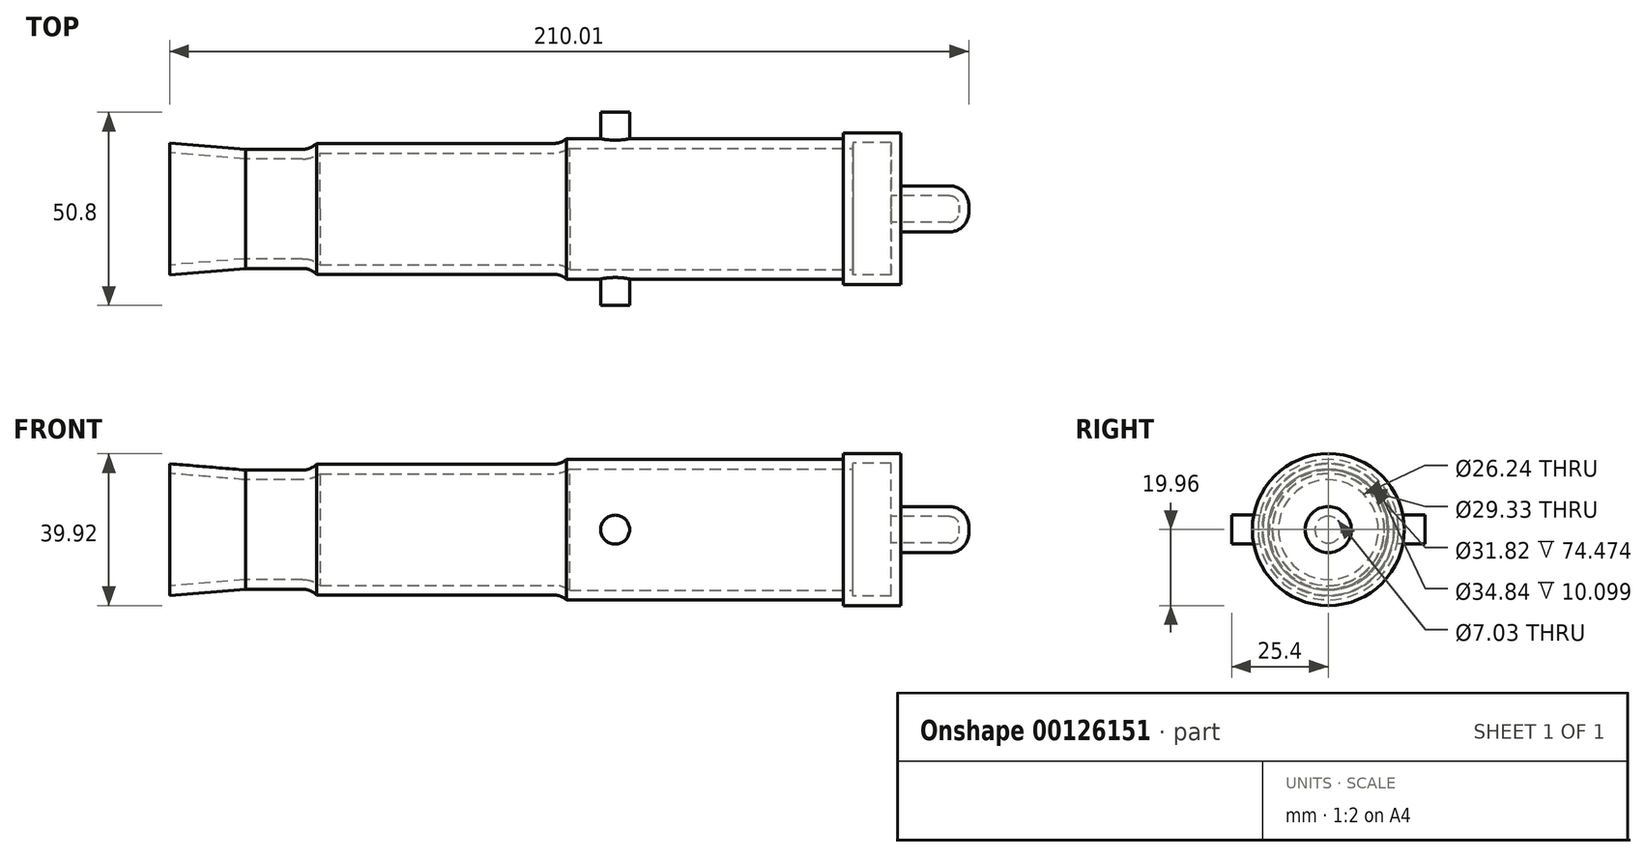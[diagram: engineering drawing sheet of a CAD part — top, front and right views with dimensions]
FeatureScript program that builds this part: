
annotation { "Feature Type Name" : "Feature", "Feature Type Description" : "" }
export const myFeature = defineFeature(function(context is Context, id is Id, definition is map)
    precondition{}
    {
        {
            var Q0;
            Q0=qCreatedBy(makeId("Right.planeOp"),FACE);
            var sketch = newSketch(context, id + "F0", { "sketchPlane" : qUnion([Q0])});
            skCircle(sketch, "E0", {"center": v(0, 0) * mm, "radius": 15.66 * mm});
            skSolve(sketch);
        }
        {
            var Q0;
            Q0 = qSketchRegion(id + "F0", true);
            extrude(context, id + "F1", {"entities" : qUnion([Q0]), "depth" : 157.22 * mm});
        }
        {
            var Q0;
            Q0=makeQuery(id+"F1.opExtrude","CAP_FACE",FACE,{"disambiguationData":[OSD([sQuery(id+"F0.wireOp",EDGE,"E0")])],"isStart":false});
            var sketch = newSketch(context, id + "F2", { "sketchPlane" : qUnion([Q0])});
            skCircle(sketch, "E1", {"center": v(0, 0) * mm, "radius": 17.2 * mm});
            skSolve(sketch);
        }
        {
            var Q0;
            Q0 = qSketchRegion(id + "F2", true);
            extrude(context, id + "F3", {"entities" : qUnion([Q0]), "operationType" : NewBodyOperationType.ADD, "oppositeDirection" : true, "depth" : 138.47 * mm});
        }
        {
            var Q0;
            Q0=makeQuery(id+"F3.boolean.opBoolean","MERGE",FACE,{"derivedFrom":[makeQuery(id+"F1.opExtrude","CAP_FACE",FACE,{"disambiguationData":[OSD([sQuery(id+"F0.wireOp",EDGE,"E0")])],"isStart":false}),makeQuery(id+"F3.opExtrude","CAP_FACE",FACE,{"disambiguationData":[OSD([sQuery(id+"F2.wireOp",EDGE,"E1")])],"isStart":true})]});
            var sketch = newSketch(context, id + "F4", { "sketchPlane" : qUnion([Q0])});
            skCircle(sketch, "E2", {"center": v(0, 0) * mm, "radius": 18.45 * mm});
            skSolve(sketch);
        }
        {
            var Q0;
            Q0 = qSketchRegion(id + "F4", true);
            extrude(context, id + "F5", {"entities" : qUnion([Q0]), "operationType" : NewBodyOperationType.ADD, "oppositeDirection" : true, "depth" : 72.78 * mm});
        }
        {
            var Q0;
            Q0=makeQuery(id+"F5.boolean.opBoolean","MERGE",FACE,{"derivedFrom":[makeQuery(id+"F3.boolean.opBoolean","MERGE",FACE,{"derivedFrom":[makeQuery(id+"F1.opExtrude","CAP_FACE",FACE,{"disambiguationData":[OSD([sQuery(id+"F0.wireOp",EDGE,"E0")])],"isStart":false}),makeQuery(id+"F3.opExtrude","CAP_FACE",FACE,{"disambiguationData":[OSD([sQuery(id+"F2.wireOp",EDGE,"E1")])],"isStart":true})]}),makeQuery(id+"F5.opExtrude","CAP_FACE",FACE,{"disambiguationData":[OSD([sQuery(id+"F4.wireOp",EDGE,"E2")])],"isStart":true})]});
            var sketch = newSketch(context, id + "F6", { "sketchPlane" : qUnion([Q0])});
            skCircle(sketch, "E3", {"center": v(0, 0) * mm, "radius": 19.96 * mm});
            skSolve(sketch);
        }
        {
            var Q0;
            Q0 = qSketchRegion(id + "F6", true);
            extrude(context, id + "F7", {"entities" : qUnion([Q0]), "operationType" : NewBodyOperationType.ADD, "depth" : 15.18 * mm});
        }
        {
            var Q0;
            Q0=makeQuery(id+"F7.opExtrude","CAP_FACE",FACE,{"disambiguationData":[OSD([sQuery(id+"F6.wireOp",EDGE,"E3")])],"isStart":false});
            var sketch = newSketch(context, id + "F8", { "sketchPlane" : qUnion([Q0])});
            skCircle(sketch, "E4", {"center": v(0, 0) * mm, "radius": 6.06 * mm});
            skSolve(sketch);
        }
        {
            var Q0;
            Q0 = qSketchRegion(id + "F8", true);
            extrude(context, id + "F9", {"entities" : qUnion([Q0]), "operationType" : NewBodyOperationType.ADD, "depth" : 17.8 * mm});
        }
        {
            var Q0;
            Q0=makeQuery(id+"F1.opExtrude","CAP_FACE",FACE,{"disambiguationData":[OSD([sQuery(id+"F0.wireOp",EDGE,"E0")])],"isStart":true});
            var sketch = newSketch(context, id + "F10", { "sketchPlane" : qUnion([Q0])});
            skCircle(sketch, "E5", {"center": v(-54.08, 12.16) * mm, "radius": 1.97 * mm});
            skSolve(sketch);
        }
        {
            var Q0;
            Q0 = qSketchRegion(id + "F10", true);
            extrude(context, id + "F11", {"entities" : qUnion([Q0]), "depth" : 19.8 * mm});
        }
        {
            var Q0;
            Q0=makeQuery(id+"F11.opExtrude","CAP_FACE",FACE,{"disambiguationData":[OSD([sQuery(id+"F10.wireOp",EDGE,"E5")])],"isStart":false});
            var sketch = newSketch(context, id + "F12", { "sketchPlane" : qUnion([Q0])});
            skCircle(sketch, "E6", {"center": v(0, 0) * mm, "radius": 17.32 * mm});
            skSolve(sketch);
        }
        {
            var Q0;
            Q0 = qSketchRegion(id + "F12", true);
            extrude(context, id + "F13", {"entities" : qUnion([Q0]), "operationType" : NewBodyOperationType.ADD, "oppositeDirection" : true, "depth" : 19.95 * mm});
        }
        {
            var Q0;
            Q0=qCreatedBy(makeId("Front.planeOp"),FACE);
            var sketch = newSketch(context, id + "F14", { "sketchPlane" : qUnion([Q0])});
            skLineSegment(sketch, "E7", {"start": v(-19.81, 17.32) * mm, "end": v(0.13, 15.66) * mm});
            skLineSegment(sketch, "E8", {"start": v(-19.81, -17.32) * mm, "end": v(0.13, -15.66) * mm});
            skLineSegment(sketch, "E9", {"start": v(0.13, -15.66) * mm, "end": v(0.13, -17.94) * mm});
            skLineSegment(sketch, "E10", {"start": v(0.13, -17.94) * mm, "end": v(-19.81, -17.32) * mm});
            skLineSegment(sketch, "E11", {"start": v(0.13, 15.66) * mm, "end": v(0.13, 17.7) * mm});
            skLineSegment(sketch, "E12", {"start": v(0.13, 17.7) * mm, "end": v(-19.81, 17.32) * mm});
            skLineSegment(sketch, "E13", {"start": v(0, 0) * mm, "end": v(-20.9, 0) * mm});
            skSolve(sketch);
        }
        {
            var Q0;
            Q0=makeQuery(id+"F14.imprint","IMPRINT",FACE,{"disambiguationData":[TD([[makeQuery(id+"F14.imprint","IMPRINT",EDGE,{"derivedFrom":sQuery(id+"F14.wireOp",EDGE,"E7")}),1.0]])]});
            var Q1;
            Q1=sQuery(id+"F14.wireOp",EDGE,"E13");
            revolve(context, id + "F15", {"operationType" : NewBodyOperationType.REMOVE, "entities" : qUnion([Q0]), "axis" : qUnion([Q1]), "revolveType" : RevolveType.FULL, "oppositeDirection" : true});
        }
        {
            var Q0;
            Q0=makeQuery(id+"F5.opExtrude","CAP_EDGE",EDGE,{"disambiguationData":[OSD([sQuery(id+"F4.wireOp",EDGE,"E2")])],"isStart":true});
            var Q1;
            Q1=makeQuery(id+"F5.boolean.opBoolean","INTERSECT",EDGE,{"derivedFrom":[makeQuery(id+"F3.opExtrude","SWEPT_FACE",FACE,{"disambiguationData":[OSD([sQuery(id+"F2.wireOp",EDGE,"E1")])]}),makeQuery(id+"F5.opExtrude","CAP_FACE",FACE,{"disambiguationData":[OSD([sQuery(id+"F4.wireOp",EDGE,"E2")])],"isStart":false})]});
            var Q2;
            Q2=makeQuery(id+"F3.boolean.opBoolean","INTERSECT",EDGE,{"derivedFrom":[makeQuery(id+"F1.opExtrude","SWEPT_FACE",FACE,{"disambiguationData":[OSD([sQuery(id+"F0.wireOp",EDGE,"E0")])]}),makeQuery(id+"F3.opExtrude","CAP_FACE",FACE,{"disambiguationData":[OSD([sQuery(id+"F2.wireOp",EDGE,"E1")])],"isStart":false})]});
            fillet(context, id + "F16", {"entities" : qUnion([Q0, Q1, Q2]), "radius" : 5.08 * mm, "tangentPropagation" : true, "allowEdgeOverflow" : false});
        }
        {
            var Q0;
            Q0=makeQuery(id+"F9.opExtrude","CAP_EDGE",EDGE,{"disambiguationData":[OSD([sQuery(id+"F8.wireOp",EDGE,"E4")])],"isStart":true});
            var Q1;
            Q1=makeQuery(id+"F9.opExtrude","CAP_EDGE",EDGE,{"disambiguationData":[OSD([sQuery(id+"F8.wireOp",EDGE,"E4")])],"isStart":false});
            fillet(context, id + "F17", {"entities" : qUnion([Q0, Q1]), "radius" : 5.08 * mm, "tangentPropagation" : true, "allowEdgeOverflow" : false});
        }
        {
            var Q0;
            Q0=makeQuery(id+"F13.opExtrude","CAP_FACE",FACE,{"disambiguationData":[OSD([sQuery(id+"F12.wireOp",EDGE,"E6")])],"isStart":true});
            var Q1;
            Q1=makeQuery(id+"F1.opExtrude","SWEPT_BODY",BODY,{"disambiguationData":[OSD([sQuery(id+"F0.wireOp",EDGE,"E0")])]});
            shell(context, id + "F18", {"entities" : qUnion([Q0]), "parts" : qUnion([Q1]), "thickness" : 2.54 * mm});
        }
        {
            var Q0;
            Q0=qCreatedBy(makeId("Front.planeOp"),FACE);
            var sketch = newSketch(context, id + "F19", { "sketchPlane" : qUnion([Q0])});
            skCircle(sketch, "E14", {"center": v(97.26, 0) * mm, "radius": 3.81 * mm});
            skSolve(sketch);
        }
        {
            var Q0;
            Q0 = qSketchRegion(id + "F19", true);
            extrude(context, id + "F20", {"entities" : qUnion([Q0]), "operationType" : NewBodyOperationType.ADD, "depth" : 25.4 * mm, "hasSecondDirection" : true, "secondDirectionOppositeDirection" : false, "secondDirectionDepth" : 17.34 * mm});
        }
        {
            var Q0;
            Q0=qCreatedBy(makeId("Front.planeOp"),FACE);
            var sketch = newSketch(context, id + "F21", { "sketchPlane" : qUnion([Q0])});
            skCircle(sketch, "E15", {"center": v(97.28, 0) * mm, "radius": 3.81 * mm});
            skSolve(sketch);
        }
        {
            var Q0;
            Q0 = qSketchRegion(id + "F21", true);
            extrude(context, id + "F22", {"entities" : qUnion([Q0]), "operationType" : NewBodyOperationType.ADD, "oppositeDirection" : true, "depth" : 25.4 * mm, "hasSecondDirection" : true, "secondDirectionOppositeDirection" : true, "secondDirectionDepth" : 16.82 * mm});
        }
        {
            var Q0;
            Q0=makeQuery(id+"F11.opExtrude","SWEPT_BODY",BODY,{"disambiguationData":[OSD([sQuery(id+"F10.wireOp",EDGE,"E5")])]});
            deleteBodies(context, id + "F23", {"entities" : qUnion([Q0])});
        }
    });
